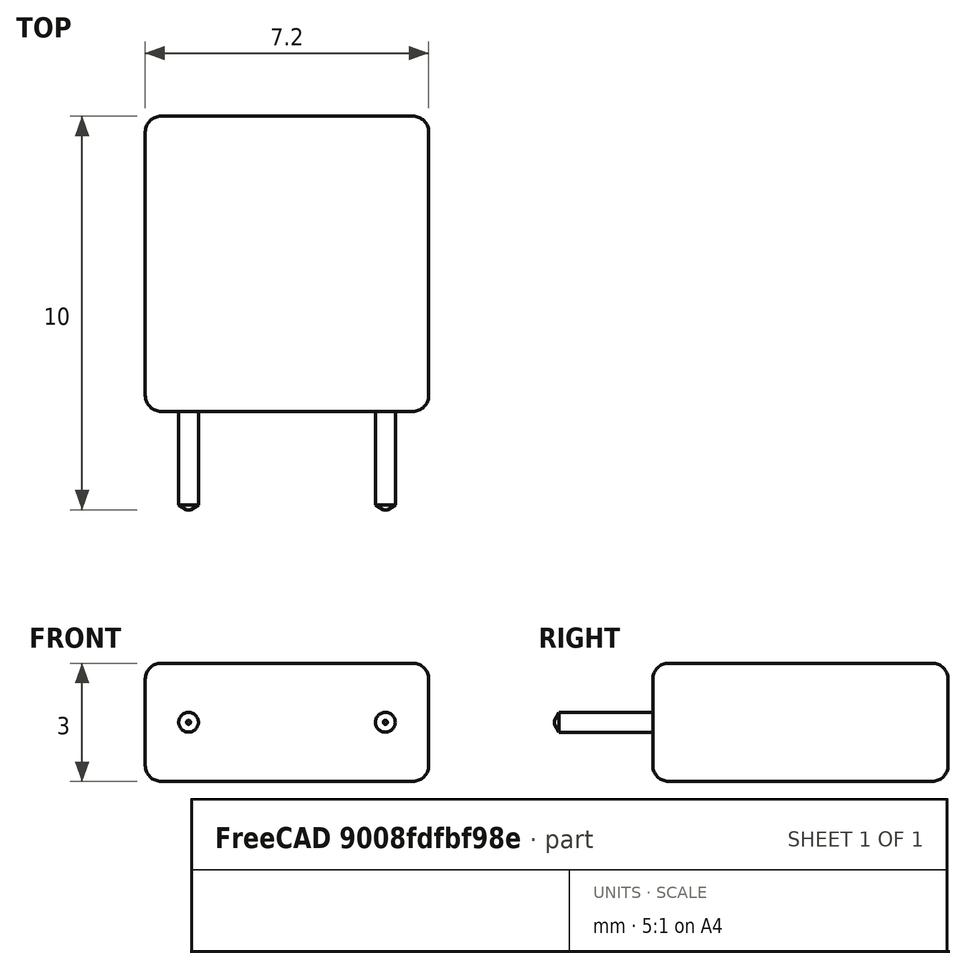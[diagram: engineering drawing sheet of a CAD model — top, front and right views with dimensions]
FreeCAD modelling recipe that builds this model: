
FCSTD DOCUMENT  (FreeCAD 0.17R13528 (Git))
Label: WIMA_B_Case
License: All rights reserved
LicenseURL: http://en.wikipedia.org/wiki/All_rights_reserved
objects: Part::Part2DObjectPython×6, Part::Feature×1
note: 7 computed .brp shape members not serialized (recipe doc carries the construction recipe); baked Part::Feature solids carry a one-line shape summary decoded from their .brp

FEATURE [Part::Part2DObjectPython] ShapeString  label="F_WIMA"  # Draft 2D object (typed FeaturePython)
  FontFile = <userpath>/Desktop/Freecad Projects/calibrib.ttf
  Placement = pos=(-0.75,3.5,1.51) rot=(0,0,1;0rad)
  Size = 1.75
  String = WIMA
  Tracking = 0
FEATURE [Part::Part2DObjectPython] ShapeString001  label="F_Vaule/Rating"  # Draft 2D object (typed FeaturePython)
  FontFile = <userpath>/Desktop/Freecad Projects/calibrib.ttf
  Placement = pos=(-0.65,2.25,1.51) rot=(0,0,1;0rad)
  Size = 1
  String = 4700/400V
  Tracking = 0
FEATURE [Part::Part2DObjectPython] ShapeString002  label="F_Tolerance"  # Draft 2D object (typed FeaturePython)
  FontFile = <userpath>/Desktop/Freecad Projects/calibrib.ttf
  Placement = pos=(-0.65,1,1.51) rot=(0,0,1;0rad)
  Size = 1
  String = 10
  Tracking = 0
FEATURE [Part::Part2DObjectPython] ShapeString003  label="B_WIMA"  # Draft 2D object (typed FeaturePython)
  FontFile = <userpath>/Desktop/Freecad Projects/calibrib.ttf
  Placement = pos=(5,3.5,-1.51) rot=(0,1,0;3.14159rad)
  Size = 1.75
  String = WIMA
  Tracking = 0
FEATURE [Part::Part2DObjectPython] ShapeString004  label="B_Value/Tolerance"  # Draft 2D object (typed FeaturePython)
  FontFile = <userpath>/Desktop/Freecad Projects/calibrib.ttf
  Placement = pos=(4.9,2.25,-1.51) rot=(0,1,0;3.14159rad)
  Size = 1
  String = 4700/400V
  Tracking = 0
FEATURE [Part::Part2DObjectPython] ShapeString005  label="B_Tolerance"  # Draft 2D object (typed FeaturePython)
  FontFile = <userpath>/Desktop/Freecad Projects/calibrib.ttf
  Placement = pos=(4.9,1,-1.51) rot=(0,1,0;3.14159rad)
  Size = 1
  String = 10
  Tracking = 0
FEATURE [Part::Feature] Part__Feature  label="WIMA_B_Case"
  shape: bbox 7.2 x 10 x 3 mm, 36 faces (baked)
